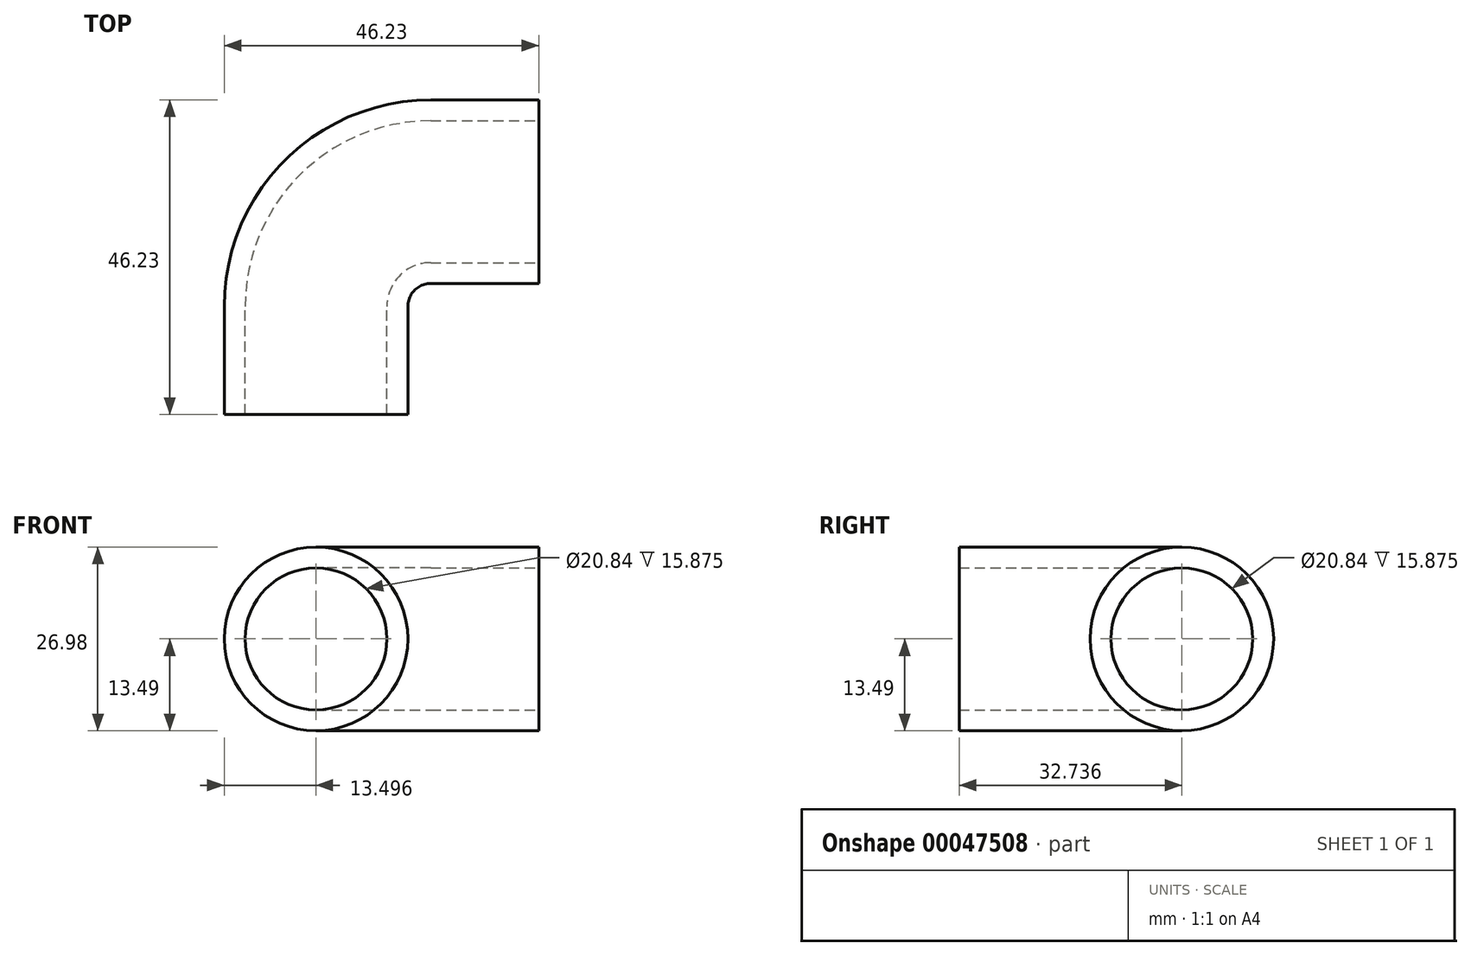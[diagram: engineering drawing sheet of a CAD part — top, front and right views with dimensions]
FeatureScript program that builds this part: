
annotation { "Feature Type Name" : "Feature", "Feature Type Description" : "" }
export const myFeature = defineFeature(function(context is Context, id is Id, definition is map)
    precondition{}
    {
        {
            var Q0;
            Q0=qCreatedBy(makeId("Top.planeOp"),FACE);
            var sketch = newSketch(context, id + "F0", { "sketchPlane" : qUnion([Q0])});
            skLineSegment(sketch, "E0", {"start": v(0, 0) * mm, "end": v(0, 15.88) * mm});
            skLineSegment(sketch, "E1", {"start": v(3.37, 19.24) * mm, "end": v(19.24, 19.24) * mm});
            skArc(sketch, "E2", {"start": v(0, 15.88) * mm, "mid": v(0.99, 18.26) * mm, "end": v(3.37, 19.24) * mm});
            skLineSegment(sketch, "E3", {"start": v(0, 15.88) * mm, "end": v(3.37, 19.24) * mm, "construction": true});
            skSolve(sketch);
        }
        {
            var Q0;
            Q0=qCreatedBy(makeId("Front.planeOp"),FACE);
            var sketch = newSketch(context, id + "F1", { "sketchPlane" : qUnion([Q0])});
            skCircle(sketch, "E4", {"center": v(-13.5, 0) * mm, "radius": 13.5 * mm});
            skLineSegment(sketch, "E5", {"start": v(0, -15.3) * mm, "end": v(0, 22.29) * mm, "construction": true});
            skSolve(sketch);
        }
        {
            var Q0;
            Q0 = qSketchRegion(id + "F1", true);
            var Q1;
            Q1 = qConstructionFilter(qBodyType(qCreatedBy(id + "F0" ,EDGE), BodyType.WIRE), ConstructionObject.NO);
            sweep(context, id + "F2", {"profiles" : qUnion([Q0]), "path" : qUnion([Q1])});
        }
        {
            var Q0;
            Q0=makeQuery(id+"F2.opSweep","CAP_FACE",FACE,{"disambiguationData":[OSD([sQuery(id+"F0.wireOp",VERTEX,"E0.start"),sQuery(id+"F1.wireOp",EDGE,"E4")])],"isStart":true});
            var Q1;
            Q1=makeQuery(id+"F2.opSweep","CAP_FACE",FACE,{"disambiguationData":[OSD([sQuery(id+"F0.wireOp",VERTEX,"E1.end"),sQuery(id+"F1.wireOp",EDGE,"E4")])],"isStart":false});
            shell(context, id + "F3", {"entities" : qUnion([Q0, Q1]), "thickness" : 3.07 * mm});
        }
    });
